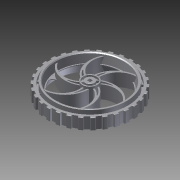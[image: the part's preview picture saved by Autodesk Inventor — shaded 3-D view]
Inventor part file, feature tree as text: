
AUTODESK INVENTOR PART (.ipt)
format: ipt  version: 2015 (Build 190159000, 159)  size: 1,414,144 bytes
history: native  units: mm (DEFAULTED — no unit token found)
features: imported_body x1, sketch x1, other x1, extrude x1
ambient origin geometry x8: Origin, YZ Plane, XZ Plane, XY Plane, X Axis, Y Axis, Z Axis, Center Point
bodies: Solid1 (feature_tree)
feature tree (4):
  imported_body  "Base1"
  sketch  "Sketch1"  dims[d0=25.4mm d1=0.0mm d2=0.0mm d3=0.0mm]
  other  "Srf1"
  extrude  "ExtrusionSrf1"  TaperAngle=0.0deg  [1 undecoded]
note: 1 required parameter value undecoded (feature->parameter linkage not recoverable at this tier; creation-order binding heuristic only, values carry confidence <= 0.55)
